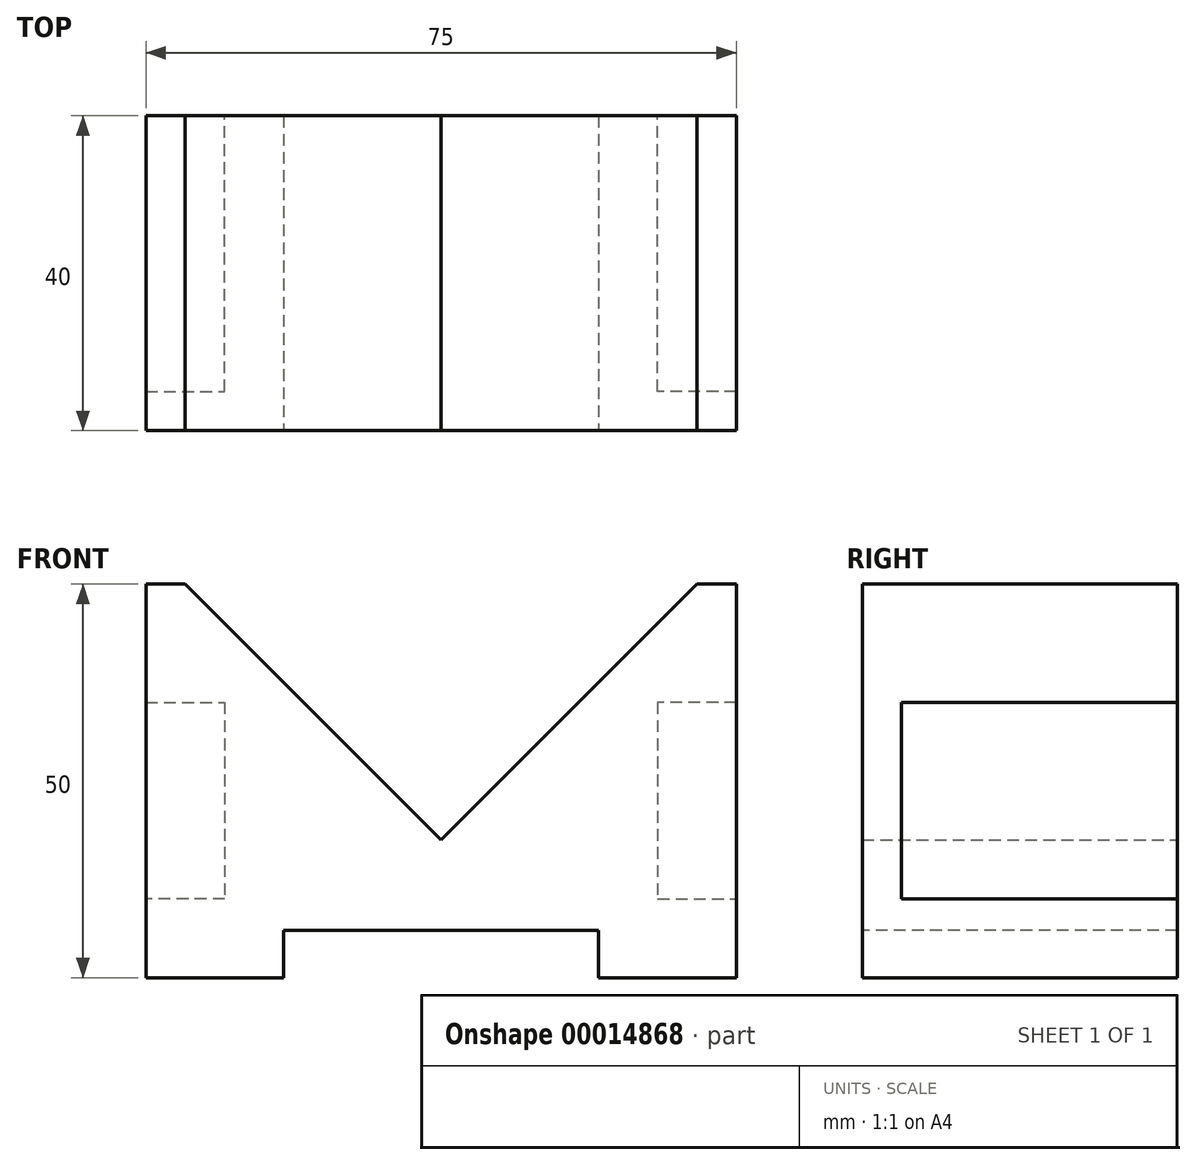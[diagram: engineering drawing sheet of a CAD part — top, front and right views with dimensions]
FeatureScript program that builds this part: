
annotation { "Feature Type Name" : "Feature", "Feature Type Description" : "" }
export const myFeature = defineFeature(function(context is Context, id is Id, definition is map)
    precondition{}
    {
        {
            var Q0;
            Q0=qCreatedBy(makeId("Front.planeOp"),FACE);
            var sketch = newSketch(context, id + "F0", { "sketchPlane" : qUnion([Q0])});
            skLineSegment(sketch, "E0", {"start": v(0, 0) * mm, "end": v(75, 0) * mm});
            skLineSegment(sketch, "E1", {"start": v(75, 0) * mm, "end": v(75, 50) * mm});
            skLineSegment(sketch, "E2", {"start": v(75, 50) * mm, "end": v(70, 50) * mm});
            skLineSegment(sketch, "E3", {"start": v(70, 50) * mm, "end": v(37.5, 17.5) * mm});
            skLineSegment(sketch, "E4", {"start": v(37.5, 17.5) * mm, "end": v(5, 50) * mm});
            skLineSegment(sketch, "E5", {"start": v(5, 50) * mm, "end": v(0, 50) * mm});
            skLineSegment(sketch, "E6", {"start": v(0, 50) * mm, "end": v(0, 0) * mm});
            skSolve(sketch);
        }
        {
            var Q0;
            Q0=makeQuery(id+"F0.imprint","IMPRINT",FACE,{"disambiguationData":[TD([[makeQuery(id+"F0.imprint","IMPRINT",EDGE,{"derivedFrom":sQuery(id+"F0.wireOp",EDGE,"E0")}),1.0]])]});
            extrude(context, id + "F1", {"entities" : qUnion([Q0]), "depth" : 40 * mm});
        }
        {
            var Q0;
            Q0=makeQuery(id+"F1.opExtrude","CAP_FACE",FACE,{"disambiguationData":[OSD([sQuery(id+"F0.wireOp",EDGE,"E0"),sQuery(id+"F0.wireOp",EDGE,"E1"),sQuery(id+"F0.wireOp",EDGE,"E2"),sQuery(id+"F0.wireOp",EDGE,"E3"),sQuery(id+"F0.wireOp",EDGE,"E4"),sQuery(id+"F0.wireOp",EDGE,"E5"),sQuery(id+"F0.wireOp",EDGE,"E6")])],"isStart":false});
            var sketch = newSketch(context, id + "F2", { "sketchPlane" : qUnion([Q0])});
            skLineSegment(sketch, "E7", {"start": v(17.5, 0) * mm, "end": v(17.5, 6) * mm});
            skLineSegment(sketch, "E8", {"start": v(17.5, 6) * mm, "end": v(57.5, 6) * mm});
            skLineSegment(sketch, "E9", {"start": v(57.5, 6) * mm, "end": v(57.5, 0) * mm});
            skSolve(sketch);
        }
        {
            var Q0;
            {var subQ2=sQuery(id+"F2.wireOp",EDGE,"E7");Q0=makeQuery(id+"F2.imprint","IMPRINT",FACE,{"disambiguationData":[TD([[makeQuery(id+"F2.imprint","IMPRINT",EDGE,{"derivedFrom":subQ2}),-1.0]])]});}
            extrude(context, id + "F3", {"entities" : qUnion([Q0]), "operationType" : NewBodyOperationType.REMOVE, "endBound" : BoundingType.UP_TO_NEXT, "oppositeDirection" : true, "depth" : 25.4 * mm});
        }
        {
            var Q0;
            Q0=makeQuery(id+"F1.opExtrude","CAP_FACE",FACE,{"disambiguationData":[OSD([sQuery(id+"F0.wireOp",EDGE,"E0"),sQuery(id+"F0.wireOp",EDGE,"E1"),sQuery(id+"F0.wireOp",EDGE,"E2"),sQuery(id+"F0.wireOp",EDGE,"E3"),sQuery(id+"F0.wireOp",EDGE,"E4"),sQuery(id+"F0.wireOp",EDGE,"E5"),sQuery(id+"F0.wireOp",EDGE,"E6")])],"isStart":true});
            var sketch = newSketch(context, id + "F4", { "sketchPlane" : qUnion([Q0])});
            skLineSegment(sketch, "E10", {"start": v(-75, 35) * mm, "end": v(-65, 35) * mm});
            skLineSegment(sketch, "E11", {"start": v(-65, 35) * mm, "end": v(-65, 10) * mm});
            skLineSegment(sketch, "E12", {"start": v(-65, 10) * mm, "end": v(-75, 10) * mm});
            skLineSegment(sketch, "E13", {"start": v(0, 35) * mm, "end": v(-10, 35) * mm});
            skLineSegment(sketch, "E14", {"start": v(-10, 35) * mm, "end": v(-10, 10) * mm});
            skLineSegment(sketch, "E15", {"start": v(-10, 10) * mm, "end": v(0, 10) * mm});
            skSolve(sketch);
        }
        {
            var Q0;
            {var subQ2=sQuery(id+"F4.wireOp",EDGE,"E10");Q0=makeQuery(id+"F4.imprint","IMPRINT",FACE,{"disambiguationData":[TD([[makeQuery(id+"F4.imprint","IMPRINT",EDGE,{"derivedFrom":subQ2}),-1.0]])]});}
            var Q1;
            {var subQ2=sQuery(id+"F4.wireOp",EDGE,"E13");Q1=makeQuery(id+"F4.imprint","IMPRINT",FACE,{"disambiguationData":[TD([[makeQuery(id+"F4.imprint","IMPRINT",EDGE,{"derivedFrom":subQ2}),1.0]])]});}
            extrude(context, id + "F5", {"entities" : qUnion([Q0, Q1]), "operationType" : NewBodyOperationType.REMOVE, "oppositeDirection" : true, "depth" : 35 * mm});
        }
    });
